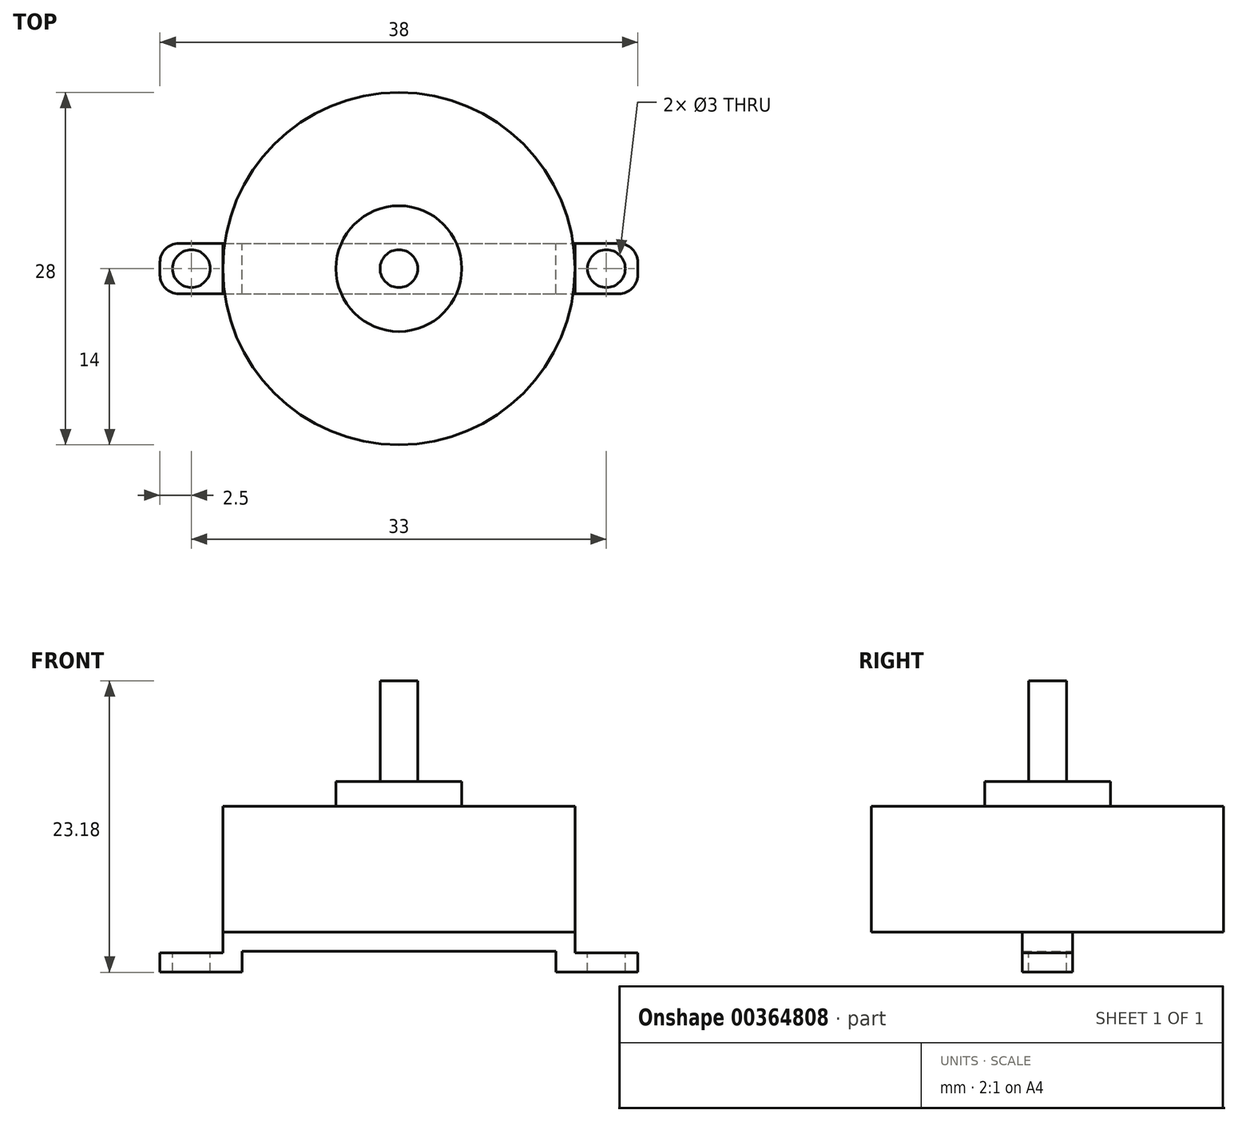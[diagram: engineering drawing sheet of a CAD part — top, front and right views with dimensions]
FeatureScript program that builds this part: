
annotation { "Feature Type Name" : "Feature", "Feature Type Description" : "" }
export const myFeature = defineFeature(function(context is Context, id is Id, definition is map)
    precondition{}
    {
        {
            var Q0;
            Q0=qCreatedBy(makeId("Top.planeOp"),FACE);
            var sketch = newSketch(context, id + "F0", { "sketchPlane" : qUnion([Q0])});
            skCircle(sketch, "E0", {"center": v(0, 0) * mm, "radius": 14 * mm});
            skSolve(sketch);
        }
        {
            var Q0;
            Q0 = qSketchRegion(id + "F0", true);
            extrude(context, id + "F1", {"entities" : qUnion([Q0]), "depth" : 10 * mm});
        }
        {
            var Q0;
            Q0=makeQuery(id+"F1.opExtrude","CAP_FACE",FACE,{"disambiguationData":[OSD([sQuery(id+"F0.wireOp",EDGE,"E0")])],"isStart":false});
            var sketch = newSketch(context, id + "F2", { "sketchPlane" : qUnion([Q0])});
            skCircle(sketch, "E1", {"center": v(0, 0) * mm, "radius": 5 * mm});
            skCircle(sketch, "E2", {"center": v(0, 0) * mm, "radius": 1.5 * mm});
            skSolve(sketch);
        }
        {
            var Q0;
            Q0=makeQuery(id+"F2.imprint","IMPRINT",FACE,{"disambiguationData":[TD([[makeQuery(id+"F2.imprint","IMPRINT",EDGE,{"derivedFrom":sQuery(id+"F2.wireOp",EDGE,"E1")}),1.0]])]});
            extrude(context, id + "F3", {"entities" : qUnion([Q0]), "operationType" : NewBodyOperationType.ADD, "depth" : 2 * mm});
        }
        {
            var Q0;
            Q0=makeQuery(id+"F3.boolean.opBoolean","SPLIT",FACE,{"disambiguationData":[TD([makeQuery(id+"F3.opExtrude","SWEPT_FACE",FACE,{"disambiguationData":[OSD([sQuery(id+"F2.wireOp",EDGE,"E2")])]})])],"derivedFrom":makeQuery(id+"F1.opExtrude","CAP_FACE",FACE,{"disambiguationData":[OSD([sQuery(id+"F0.wireOp",EDGE,"E0")])],"isStart":false})});
            extrude(context, id + "F4", {"entities" : qUnion([Q0]), "operationType" : NewBodyOperationType.ADD, "depth" : 10 * mm});
        }
        {
            var Q0;
            Q0=qCreatedBy(makeId("Front.planeOp"),FACE);
            var sketch = newSketch(context, id + "F5", { "sketchPlane" : qUnion([Q0])});
            skLineSegment(sketch, "E3.bottom", {"start": v(-14, 0) * mm, "end": v(14, 0) * mm});
            skLineSegment(sketch, "E3.top", {"start": v(-14, -1.52) * mm, "end": v(14, -1.52) * mm});
            skLineSegment(sketch, "E3.left", {"start": v(-14, 0) * mm, "end": v(-14, -1.52) * mm});
            skLineSegment(sketch, "E3.right", {"start": v(14, 0) * mm, "end": v(14, -1.52) * mm});
            skLineSegment(sketch, "E4", {"start": v(-14, -1.52) * mm, "end": v(-14, -3.17) * mm});
            skLineSegment(sketch, "E5", {"start": v(-14, -3.17) * mm, "end": v(-12.48, -3.17) * mm});
            skLineSegment(sketch, "E6", {"start": v(-12.48, -3.18) * mm, "end": v(-12.48, -1.52) * mm});
            skLineSegment(sketch, "E7", {"start": v(12.48, -1.52) * mm, "end": v(12.48, -3.18) * mm});
            skLineSegment(sketch, "E8", {"start": v(14, -1.52) * mm, "end": v(14, -3.17) * mm});
            skLineSegment(sketch, "E9", {"start": v(12.48, -3.18) * mm, "end": v(14, -3.18) * mm});
            skLineSegment(sketch, "E10.bottom", {"start": v(-14, -3.17) * mm, "end": v(-19, -3.17) * mm});
            skLineSegment(sketch, "E10.top", {"start": v(-14, -1.65) * mm, "end": v(-19, -1.65) * mm});
            skLineSegment(sketch, "E10.left", {"start": v(-14, -3.17) * mm, "end": v(-14, -1.65) * mm});
            skLineSegment(sketch, "E10.right", {"start": v(-19, -3.17) * mm, "end": v(-19, -1.65) * mm});
            skLineSegment(sketch, "E11.bottom", {"start": v(14, -3.18) * mm, "end": v(19, -3.18) * mm});
            skLineSegment(sketch, "E11.top", {"start": v(14, -1.65) * mm, "end": v(19, -1.65) * mm});
            skLineSegment(sketch, "E11.left", {"start": v(14, -3.17) * mm, "end": v(14, -1.65) * mm});
            skLineSegment(sketch, "E11.right", {"start": v(19, -3.17) * mm, "end": v(19, -1.65) * mm});
            skSolve(sketch);
        }
        {
            var Q0;
            Q0=makeQuery(id+"F5.imprint","IMPRINT",FACE,{"disambiguationData":[TD([[makeQuery(id+"F5.imprint","IMPRINT",EDGE,{"derivedFrom":sQuery(id+"F5.wireOp",EDGE,"E3.bottom")}),-1.0]])]});
            var Q1;
            {var subQ1=sQuery(id+"F5.wireOp",EDGE,"E4");Q1=makeQuery(id+"F5.imprint","IMPRINT",FACE,{"disambiguationData":[TD([[makeQuery(id+"F5.imprint","IMPRINT",EDGE,{"derivedFrom":subQ1}),1.0]])]});}
            var Q2;
            Q2=makeQuery(id+"F5.imprint","IMPRINT",FACE,{"disambiguationData":[TD([[makeQuery(id+"F5.imprint","IMPRINT",EDGE,{"derivedFrom":sQuery(id+"F5.wireOp",EDGE,"E10.bottom")}),-1.0]])]});
            var Q3;
            {var subQ1=sQuery(id+"F5.wireOp",EDGE,"E7");Q3=makeQuery(id+"F5.imprint","IMPRINT",FACE,{"disambiguationData":[TD([[makeQuery(id+"F5.imprint","IMPRINT",EDGE,{"derivedFrom":subQ1}),1.0]])]});}
            var Q4;
            Q4=makeQuery(id+"F5.imprint","IMPRINT",FACE,{"disambiguationData":[TD([[makeQuery(id+"F5.imprint","IMPRINT",EDGE,{"derivedFrom":sQuery(id+"F5.wireOp",EDGE,"E11.bottom")}),1.0]])]});
            extrude(context, id + "F6", {"entities" : qUnion([Q0, Q1, Q2, Q3, Q4]), "operationType" : NewBodyOperationType.ADD, "endBound" : BoundingType.SYMMETRIC, "depth" : 4 * mm});
        }
        {
            var Q0;
            Q0=makeQuery(id+"F6.opExtrude","SWEPT_FACE",FACE,{"disambiguationData":[OSD([sQuery(id+"F5.wireOp",EDGE,"E10.top")])]});
            var sketch = newSketch(context, id + "F7", { "sketchPlane" : qUnion([Q0])});
            skCircle(sketch, "E12", {"center": v(-16.5, 0) * mm, "radius": 1.5 * mm});
            skCircle(sketch, "E13", {"center": v(16.5, 0) * mm, "radius": 1.5 * mm});
            skLineSegment(sketch, "E14", {"start": v(0, 0) * mm, "end": v(-16.5, 0) * mm});
            skLineSegment(sketch, "E15", {"start": v(0, 0) * mm, "end": v(16.5, 0) * mm});
            skSolve(sketch);
        }
        {
            var Q0;
            Q0=makeQuery(id+"F7.imprint","IMPRINT",FACE,{"disambiguationData":[TD([[makeQuery(id+"F7.imprint","IMPRINT",EDGE,{"derivedFrom":sQuery(id+"F7.wireOp",EDGE,"E12")}),1.0]])]});
            var Q1;
            Q1=makeQuery(id+"F7.imprint","IMPRINT",FACE,{"disambiguationData":[TD([[makeQuery(id+"F7.imprint","IMPRINT",EDGE,{"derivedFrom":sQuery(id+"F7.wireOp",EDGE,"E13")}),1.0]])]});
            extrude(context, id + "F8", {"entities" : qUnion([Q0, Q1]), "operationType" : NewBodyOperationType.REMOVE, "oppositeDirection" : true, "depth" : 25.4 * mm});
        }
        {
            var Q0;
            Q0=makeQuery(id+"F6.opExtrude","CAP_EDGE",EDGE,{"disambiguationData":[OSD([sQuery(id+"F5.wireOp",EDGE,"E10.right")])],"isStart":false});
            var Q1;
            Q1=makeQuery(id+"F6.opExtrude","CAP_EDGE",EDGE,{"disambiguationData":[OSD([sQuery(id+"F5.wireOp",EDGE,"E10.right")])],"isStart":true});
            var Q2;
            Q2=makeQuery(id+"F6.opExtrude","CAP_EDGE",EDGE,{"disambiguationData":[OSD([sQuery(id+"F5.wireOp",EDGE,"E11.right")])],"isStart":false});
            var Q3;
            Q3=makeQuery(id+"F6.opExtrude","CAP_EDGE",EDGE,{"disambiguationData":[OSD([sQuery(id+"F5.wireOp",EDGE,"E11.right")])],"isStart":true});
            fillet(context, id + "F9", {"entities" : qUnion([Q0, Q1, Q2, Q3]), "radius" : 1.5 * mm, "tangentPropagation" : true, "allowEdgeOverflow" : false});
        }
    });
